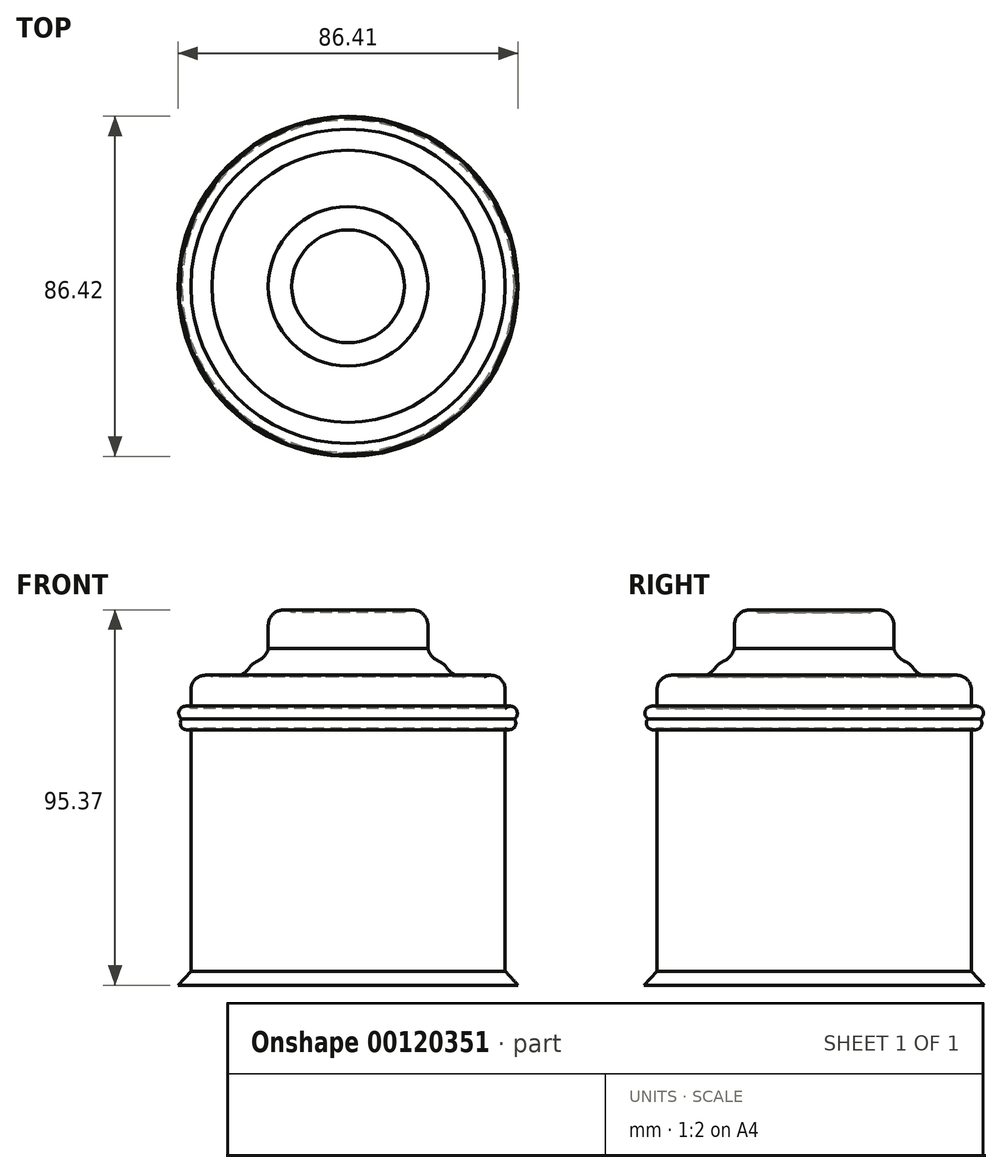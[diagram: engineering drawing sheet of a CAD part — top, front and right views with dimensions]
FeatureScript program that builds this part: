
annotation { "Feature Type Name" : "Feature", "Feature Type Description" : "" }
export const myFeature = defineFeature(function(context is Context, id is Id, definition is map)
    precondition{}
    {
        {
            var Q0;
            Q0=qCreatedBy(makeId("Front.planeOp"),FACE);
            var sketch = newSketch(context, id + "F0", { "sketchPlane" : qUnion([Q0])});
            skArc(sketch, "E0", {"start": v(25.63, 40.97) * mm, "mid": v(28.32, 42.31) * mm, "end": v(25.63, 43.66) * mm});
            skArc(sketch, "E1", {"start": v(25.63, 43.66) * mm, "mid": v(28.71, 44.85) * mm, "end": v(25.63, 46.04) * mm});
            skLineSegment(sketch, "E2", {"start": v(25.63, 46.04) * mm, "end": v(25.63, 50.8) * mm});
            skArc(sketch, "E3", {"start": v(25.63, 50.8) * mm, "mid": v(23.86, 53.95) * mm, "end": v(20.26, 54.08) * mm});
            skLineSegment(sketch, "E4", {"start": v(20.26, 54.08) * mm, "end": v(15.2, 54.08) * mm});
            skArc(sketch, "E5", {"start": v(10.13, 57.66) * mm, "mid": v(12.1, 55.07) * mm, "end": v(15.2, 54.08) * mm});
            skArc(sketch, "E6", {"start": v(5.96, 61.24) * mm, "mid": v(7.5, 58.81) * mm, "end": v(10.13, 57.66) * mm});
            skLineSegment(sketch, "E7", {"start": v(5.96, 61.24) * mm, "end": v(5.96, 67.2) * mm});
            skArc(sketch, "E8", {"start": v(5.96, 67.2) * mm, "mid": v(3.95, 70.6) * mm, "end": v(0, 70.47) * mm});
            skLineSegment(sketch, "E9", {"start": v(0, 70.47) * mm, "end": v(-14.3, 70.47) * mm});
            skLineSegment(sketch, "E10", {"start": v(-14.3, 70.47) * mm, "end": v(-14.3, -24.29) * mm});
            skLineSegment(sketch, "E11", {"start": v(25.63, 40.97) * mm, "end": v(25.63, -20.71) * mm});
            skLineSegment(sketch, "E12", {"start": v(25.63, -20.71) * mm, "end": v(28.9, -24.29) * mm});
            skLineSegment(sketch, "E13", {"start": v(28.9, -24.29) * mm, "end": v(-14.3, -24.29) * mm});
            skSolve(sketch);
        }
        {
            var Q0;
            Q0 = qSketchRegion(id + "F0", true);
            var Q1;
            Q1=sQuery(id+"F0.wireOp",EDGE,"E10");
            revolve(context, id + "F1", {"entities" : qUnion([Q0]), "axis" : qUnion([Q1]), "revolveType" : RevolveType.FULL});
        }
        {
            var Q0;
            Q0=makeQuery(id+"F1.opRevolve","SWEPT_EDGE",EDGE,{"disambiguationData":[OSD([sQuery(id+"F0.wireOp",EDGE,"E5"),sQuery(id+"F0.wireOp",EDGE,"E6")])]});
            fillet(context, id + "F2", {"entities" : qUnion([Q0]), "radius" : 5.08 * mm, "tangentPropagation" : true, "allowEdgeOverflow" : false});
        }
    });
